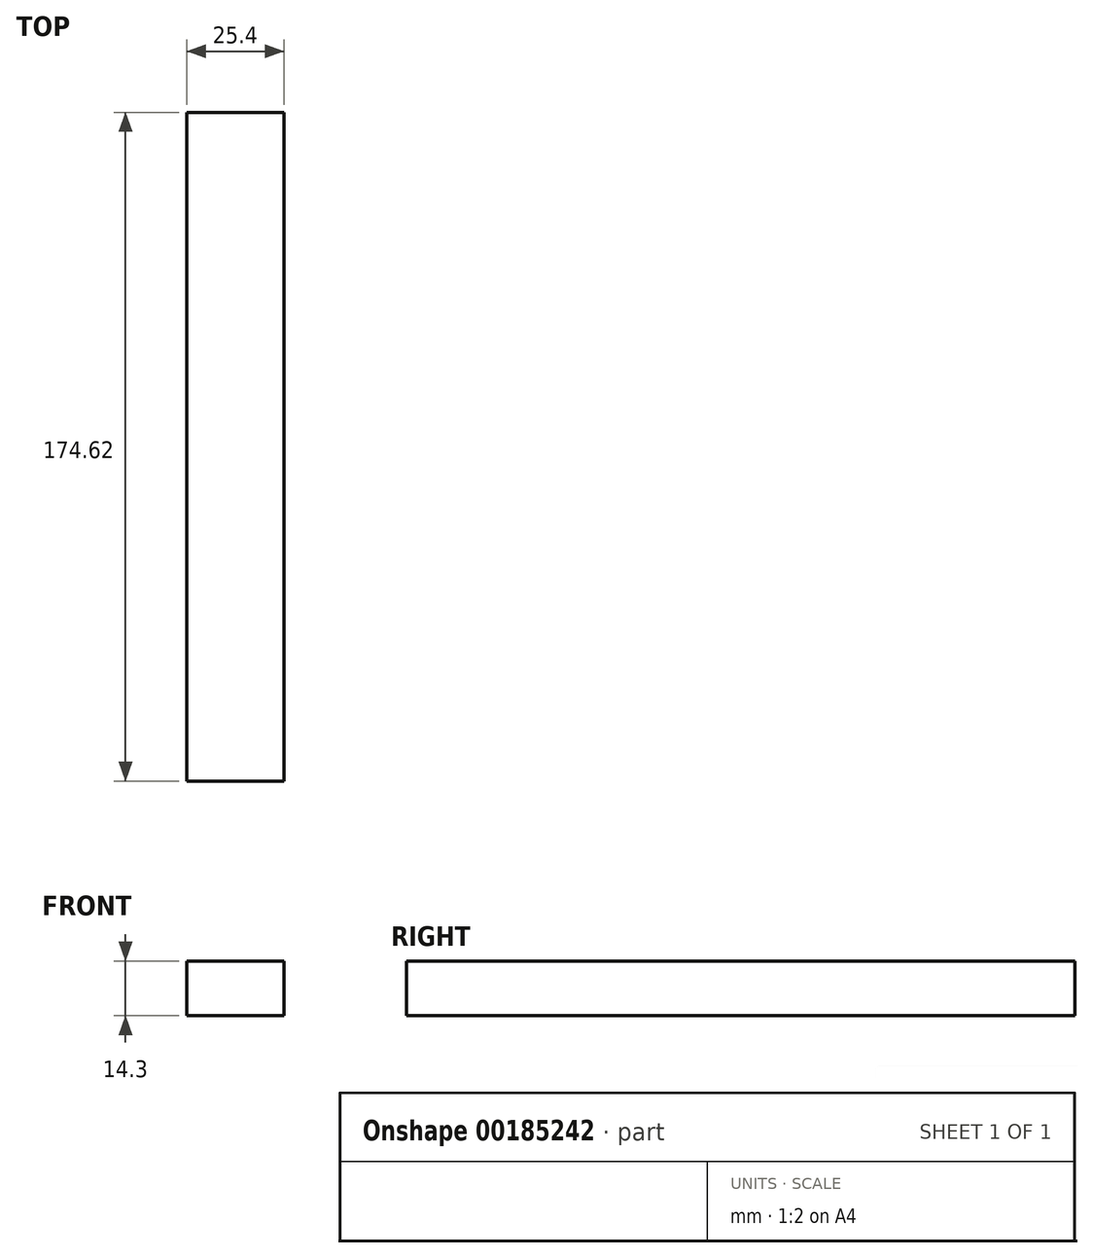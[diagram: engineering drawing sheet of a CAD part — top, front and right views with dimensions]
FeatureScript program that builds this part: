
annotation { "Feature Type Name" : "Feature", "Feature Type Description" : "" }
export const myFeature = defineFeature(function(context is Context, id is Id, definition is map)
    precondition{}
    {
        {
            var Q0;
            Q0=qCreatedBy(makeId("Right.planeOp"),FACE);
            var sketch = newSketch(context, id + "F0", { "sketchPlane" : qUnion([Q0])});
            skLineSegment(sketch, "E0.bottom", {"start": v(87.31, -7.15) * mm, "end": v(-87.31, -7.15) * mm});
            skLineSegment(sketch, "E0.top", {"start": v(87.31, 7.15) * mm, "end": v(-87.31, 7.15) * mm});
            skLineSegment(sketch, "E0.left", {"start": v(87.31, -7.15) * mm, "end": v(87.31, 7.15) * mm});
            skLineSegment(sketch, "E0.right", {"start": v(-87.31, -7.15) * mm, "end": v(-87.31, 7.15) * mm});
            skPoint(sketch, "E0.middle", {"position": v(0, 0) * mm});
            skSolve(sketch);
        }
        {
            var Q0;
            Q0=makeQuery(id+"F0.imprint","IMPRINT",FACE,{"disambiguationData":[TD([[makeQuery(id+"F0.imprint","IMPRINT",EDGE,{"derivedFrom":sQuery(id+"F0.wireOp",EDGE,"E0.bottom")}),-1.0]])]});
            extrude(context, id + "F1", {"entities" : qUnion([Q0]), "depth" : 12.7 * mm, "hasSecondDirection" : true, "secondDirectionOppositeDirection" : true, "secondDirectionDepth" : 12.7 * mm});
        }
    });
